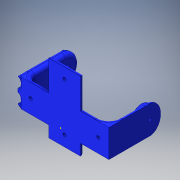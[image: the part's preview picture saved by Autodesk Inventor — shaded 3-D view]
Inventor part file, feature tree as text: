
AUTODESK INVENTOR PART (.ipt)
format: ipt  version: 2016 (Build 200138000, 138)  size: 609,280 bytes
history: native  units: in
note: dims shown in document units (in); Inventor stores cm internally (conversion verified against a paired STEP export)
features: sketch x13, extrude x12, fillet x12, hole x2
ambient origin geometry x8: Origin, YZ Plane, XZ Plane, XY Plane, X Axis, Y Axis, Z Axis, Center Point
bodies: Solid1 (feature_tree)
feature tree (39):
  extrude  "Extrusion1"  Depth=0.5197in
  extrude  "Extrusion3"  Depth=0.0787in
  sketch  "Sketch5"  dims[d9=0.9449in d10=0.0in d11=0.2835in]
  extrude  "Extrusion4"  Depth=0.2835in
  extrude  "Extrusion5"  Depth=0.2598in
  fillet  "Fillet1"  Radius=0.2598in
  fillet  "Fillet4"  Radius=0.5197in
  fillet  "Fillet5"  Radius=0.3622in
  fillet  "Fillet6"  Radius=0.1437in
  fillet  "Fillet7"  Radius=0.2224in
  extrude  "Extrusion6"  Depth=0.0787in
  sketch  "Sketch9"  dims[d24=0.0787in d25=0.0in d27=0.0787in]
  extrude  "Extrusion7"  Depth=0.0197in
  fillet  "Fillet10"  Radius=0.0197in
  fillet  "Fillet11"  Radius=0.0394in
  sketch  "Sketch10"  dims[d28=0.0787in d29=0.0in d30=0.1969in d33=0.0197in d34=0.0394in]
  extrude  "Extrusion8"  Depth=0.0197in
  extrude  "Extrusion10"  Depth=0.9449in TaperAngle=0.0deg
  extrude  "Extrusion11"  Depth=0.2598in
  sketch  "Sketch17"  dims[d43=0.2598in d44=0.2598in]
  hole  "Hole2"  [1 undecoded]
  fillet  "Fillet18"  Radius=0.1772in
  extrude  "Extrusion12"  Depth=0.0197in
  extrude  "Extrusion13"  Depth=0.1181in TaperAngle=0.0deg
  fillet  "Fillet22"  Radius=0.5906in
  hole  "Hole3"  [1 undecoded]
  extrude  "Extrusion15"  Depth=0.0197in TaperAngle=0.0deg
  fillet  "Fillet24"  Radius=0.5315in
  fillet  "Fillet25"  Radius=0.2096in
  fillet  "Fillet26"  Radius=0.1181in
  sketch  "Sketch21"  dims[d83=0.5315in d84=0.5315in d85=0.562in d86=0.0in d87=0.5315in d88=0.2096in d89=0.0in d90=0.0591in d91=0.2362in d92=0.1575in d93=0.0787in d94=90.0deg d95=0.315in d96=0.8108in d98=0.1181in d99=0.5591in d100=0.5591in d101=0.5591in d103=0.4291in d104=0.0in d106=0.0591in d107=0.4291in d108=0.0in d111=0.0748in d112=0.0591in d113=0.2362in d114=0.1575in d115=0.0787in d116=90.0deg d117=0.315in d118=0.8108in d124=0.0591in d125=0.0591in d126=0.0in d127=0.0787in d128=0.0197in d129=0.0197in d130=0.2953in d131=0.2953in d132=0.1969in d133=0.2953in d134=0.2953in d135=0.1969in d136=0.1969in d137=0.1969in d138=0.2598in d139=0.2598in d140=0.2598in d141=0.2598in]
  sketch  "Sketch1"  dims[d0=1.6535in d1=0.5197in]
  sketch  "Sketch4"  dims[d2=0.0787in d3=0.0in d8=0.0787in]
  sketch  "Sketch7"  dims[d12=0.2598in d13=0.2598in d14=0.2598in d15=0.5197in d16=0.3622in d17=0.1437in d19=0.2224in]
  sketch  "Sketch15"  dims[d35=0.0394in d36=0.0197in]
  sketch  "Sketch16"  dims[d37=0.0787in d38=0.9449in d39=0.0in]
  sketch  "Sketch18"  dims[d45=0.2598in d46=0.1181in d47=0.1772in d48=0.0in]
  sketch  "Sketch19"  dims[d49=0.0394in d50=0.0197in]
  sketch  "Sketch20"  dims[d51=0.1181in d52=0.1181in d53=0.0in d82=0.5906in]
note: 2 required parameter values undecoded (feature->parameter linkage not recoverable at this tier; creation-order binding heuristic only, values carry confidence <= 0.55)
